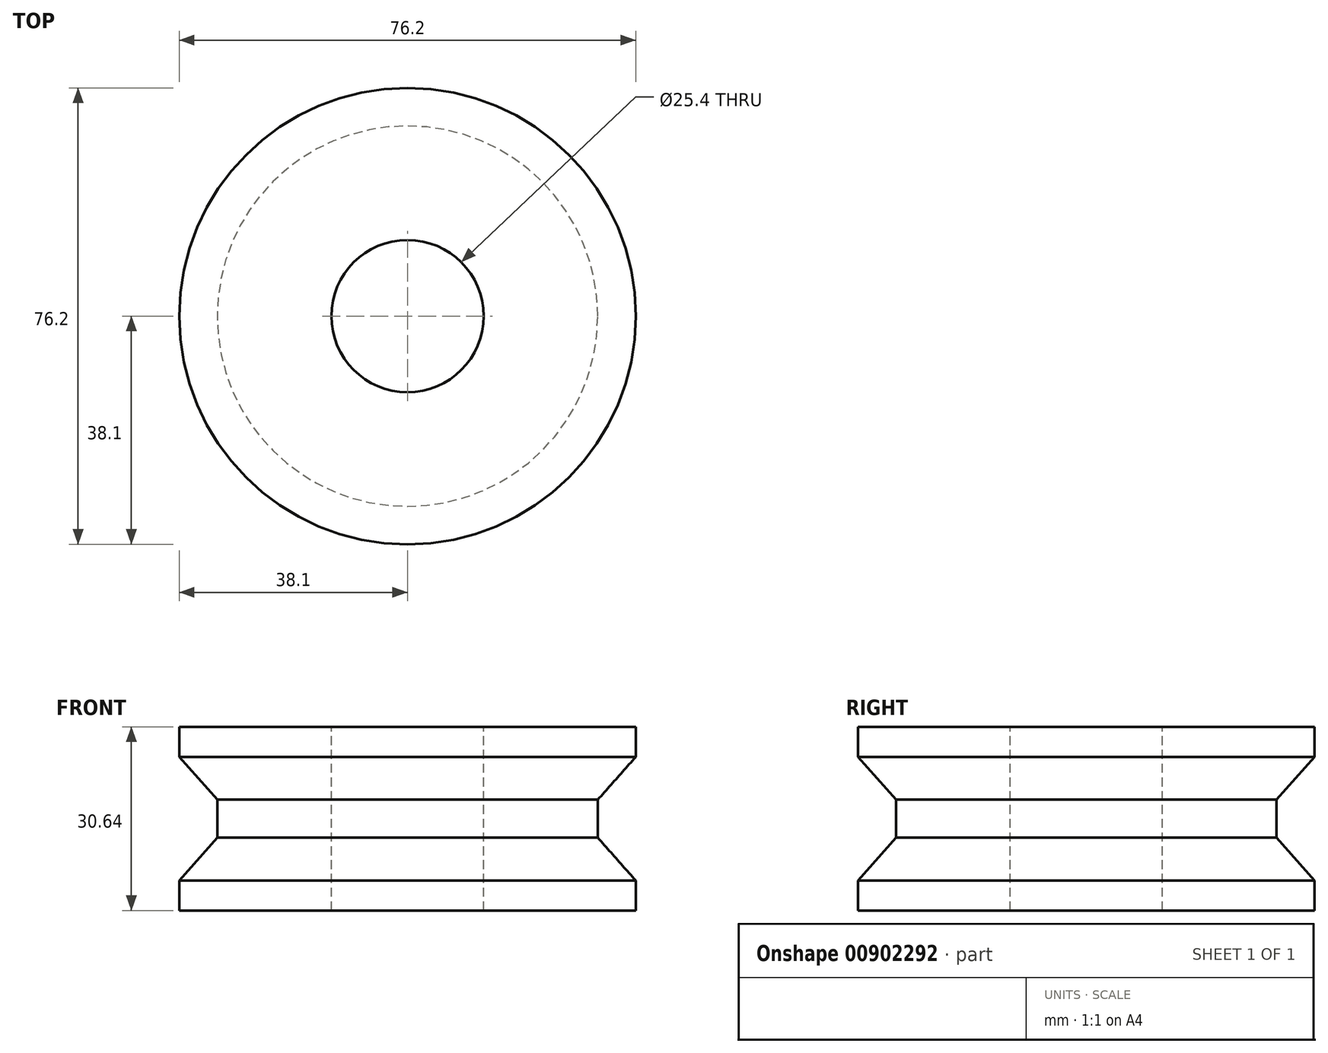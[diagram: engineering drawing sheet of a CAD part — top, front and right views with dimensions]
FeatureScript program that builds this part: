
annotation { "Feature Type Name" : "Feature", "Feature Type Description" : "" }
export const myFeature = defineFeature(function(context is Context, id is Id, definition is map)
    precondition{}
    {
        {
            var Q0;
            Q0=qCreatedBy(makeId("Right.planeOp"),FACE);
            var sketch = newSketch(context, id + "F0", { "sketchPlane" : qUnion([Q0])});
            skLineSegment(sketch, "E0", {"start": v(31.75, -3.18) * mm, "end": v(31.75, 3.18) * mm});
            skLineSegment(sketch, "E1", {"start": v(31.75, 3.17) * mm, "end": v(38.1, 10.32) * mm});
            skLineSegment(sketch, "E2", {"start": v(31.75, -3.18) * mm, "end": v(38.1, -10.32) * mm});
            skLineSegment(sketch, "E3", {"start": v(38.1, 10.32) * mm, "end": v(38.1, 15.32) * mm});
            skLineSegment(sketch, "E4", {"start": v(38.1, 15.32) * mm, "end": v(0, 15.32) * mm});
            skLineSegment(sketch, "E5", {"start": v(0, 15.32) * mm, "end": v(0, -15.32) * mm});
            skLineSegment(sketch, "E6", {"start": v(38.1, -10.32) * mm, "end": v(38.1, -15.32) * mm});
            skLineSegment(sketch, "E7", {"start": v(38.1, -15.32) * mm, "end": v(0, -15.32) * mm});
            skSolve(sketch);
        }
        {
            var Q0;
            Q0=makeQuery(id+"F0.imprint","IMPRINT",FACE,{"disambiguationData":[TD([[makeQuery(id+"F0.imprint","IMPRINT",EDGE,{"derivedFrom":sQuery(id+"F0.wireOp",EDGE,"E0")}),1.0]])]});
            var Q1;
            Q1=sQuery(id+"F0.wireOp",EDGE,"E5");
            revolve(context, id + "F1", {"surfaceOperationType" : NewSurfaceOperationType.NEW, "entities" : qUnion([Q0]), "axis" : qUnion([Q1]), "revolveType" : RevolveType.FULL});
        }
        {
            var Q0;
            Q0=makeQuery(id+"F1.opRevolve","SWEPT_FACE",FACE,{"disambiguationData":[OSD([sQuery(id+"F0.wireOp",EDGE,"E4")])]});
            var sketch = newSketch(context, id + "F2", { "sketchPlane" : qUnion([Q0])});
            skPoint(sketch, "E8", {"position": v(0, 0) * mm});
            skCircle(sketch, "E9", {"center": v(0, 0) * mm, "radius": 12.7 * mm});
            skSolve(sketch);
        }
        {
            var Q0;
            Q0=makeQuery(id+"F2.imprint","IMPRINT",FACE,{"disambiguationData":[TD([[makeQuery(id+"F2.imprint","IMPRINT",EDGE,{"derivedFrom":sQuery(id+"F2.wireOp",EDGE,"E9")}),1.0]])]});
            extrude(context, id + "F3", {"entities" : qUnion([Q0]), "operationType" : NewBodyOperationType.REMOVE, "endBound" : BoundingType.THROUGH_ALL, "oppositeDirection" : true, "depth" : 25.4 * mm, "offsetDistance" : 25.4 * mm});
        }
    });
